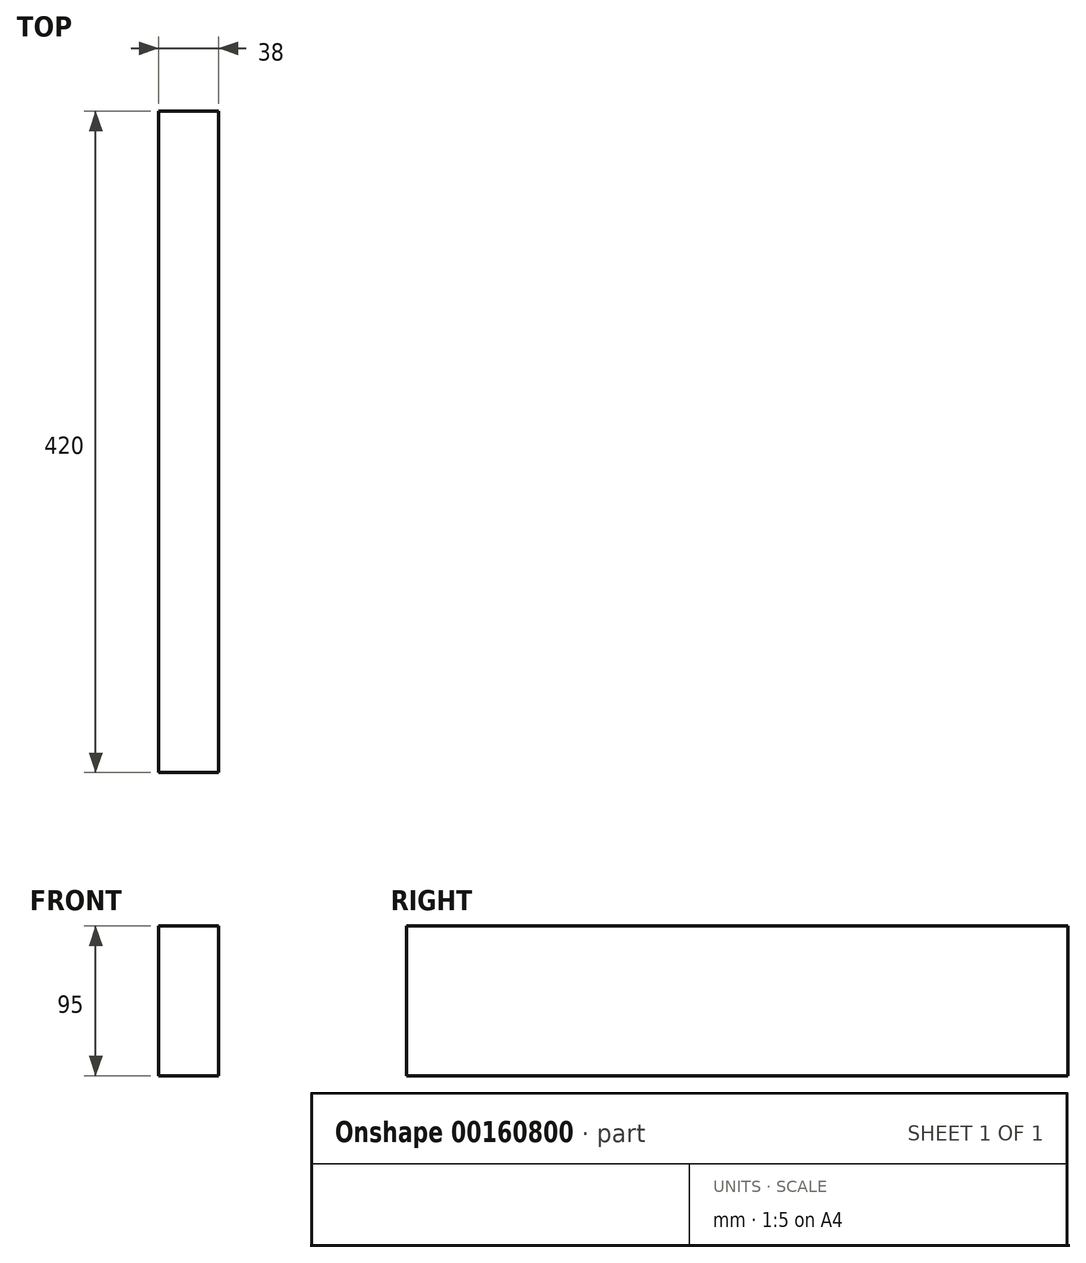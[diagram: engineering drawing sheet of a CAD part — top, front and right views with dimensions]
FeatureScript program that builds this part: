
annotation { "Feature Type Name" : "Feature", "Feature Type Description" : "" }
export const myFeature = defineFeature(function(context is Context, id is Id, definition is map)
    precondition{}
    {
        {
            var Q0;
            Q0=qCreatedBy(makeId("Front.planeOp"),FACE);
            var sketch = newSketch(context, id + "F0", { "sketchPlane" : qUnion([Q0])});
            skLineSegment(sketch, "E0.bottom", {"start": v(-104.37, 30.27) * mm, "end": v(-66.37, 30.27) * mm});
            skLineSegment(sketch, "E0.top", {"start": v(-104.37, -64.73) * mm, "end": v(-66.37, -64.73) * mm});
            skLineSegment(sketch, "E0.left", {"start": v(-104.37, 30.27) * mm, "end": v(-104.37, -64.73) * mm});
            skLineSegment(sketch, "E0.right", {"start": v(-66.37, 30.27) * mm, "end": v(-66.37, -64.73) * mm});
            skSolve(sketch);
        }
        {
            var Q0;
            Q0=makeQuery(id+"F0.imprint","IMPRINT",FACE,{"disambiguationData":[TD([[makeQuery(id+"F0.imprint","IMPRINT",EDGE,{"derivedFrom":sQuery(id+"F0.wireOp",EDGE,"E0.bottom")}),-1.0]])]});
            extrude(context, id + "F1", {"entities" : qUnion([Q0]), "depth" : 420 * mm});
        }
    });
